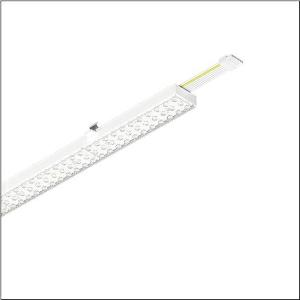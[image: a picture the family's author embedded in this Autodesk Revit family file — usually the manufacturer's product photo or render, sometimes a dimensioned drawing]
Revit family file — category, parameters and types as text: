
# Revit family: trunking_flex_31_51re12mc48b005
name_source: partatom
category: Lighting Fixtures
units: mm (PartAtom-declared; Revit-internal decimal feet)

## family parameters
Cut with Voids When Loaded = No
Host = Face
Light Source = No
Part Type = Normal
Room Calculation Point = No
Round Connector Dimension = Use Diameter
Shared = No

## types (1)
- --- (1 x LED, 8000 lm, 50 W, 4000K)
    Apparent Load = 50 VA
    CIE Flux Codes = 65 91 98 99 100
    Color Rendering = 80
    Color Temperature = 4000K
    Default Elevation = 1800 mm
    Description = Trunking Flex 31, luminaire insert, of extruded aluminium section, coated, traffic white (RAL 9016), length: 1.438mm, width: 91mm, height: 53mm, LED rated luminous flux: 8.000lm, light colour: 840, control gear: ON/OFF Multilumen, with system connector: socket, through-wiring: 5x 2.5mm², mains connection: 220..240V, AC, 50/60Hz, rated input power: 50W, connected load according to luminous flux setting (25/34/42/50W), luminous flux adjustable on luminaire in four steps (4130/5610/6850/8000lm), primary light control with lens, of plastic, primary optical cover: cover, of PMMA, light emission: direct distribution, protection rating (complete): IP20, insulation class (complete): insulation class I (protective earthing), certification: CE, UKCA, impact resistance: IK02, permissible ambient temperature for indoor applications: -20..+40°C, packaging unit: 1 piece
    Height = 58 mm
    Lamp = 1 x LED
    Lamp Light Flux = 8000 lm
    Lamp Power = 50 W
    Lamp count = 1
    Length = 1438 mm
    Luminous efficacy = 160 lm/W
    Manufacturer = Siteco
    ModVariant = No
    Model = 51RE12MC48B005
    Mounting Place = Ceiling
    Mounting Type = Pendant
    Number of Poles = 1
    OnlyDefault = Yes
    Power Factor = 1
    Product Name = Trunking Flex 31
    Product group = luminaire insert
    ProductGroupID = 901
    Protection Class = Protection class I
    Protection Degree = IP 20
    RLX_Detail_Level = 1
    RLX_Emergency_Light_Flux = 0 lm
    RLX_Emergency_Type = 0
    RLX_Emergency_Type_DB = No
    RlxData = <blob elided: 23009 chars, md5=a505bce2>
    Socket = socket
    Standby Power = 0 W
    System Light Flux = 8000 lm
    System Power = 50 W
    Type Comments = factory setting: luminous flux: 100 % | (ON | ON) | 300 mA
    Type Image = l_1297860.jpg
    URL = http://relux.com
    VarID = @adj_053894
    Voltage = 0 V
    Weight = 0.00 kg
    Width = 65 mm

## geometry (parser evidence)
native form markers: Blend x4, Sweep x13
no freeform markers — native parametric forms only
